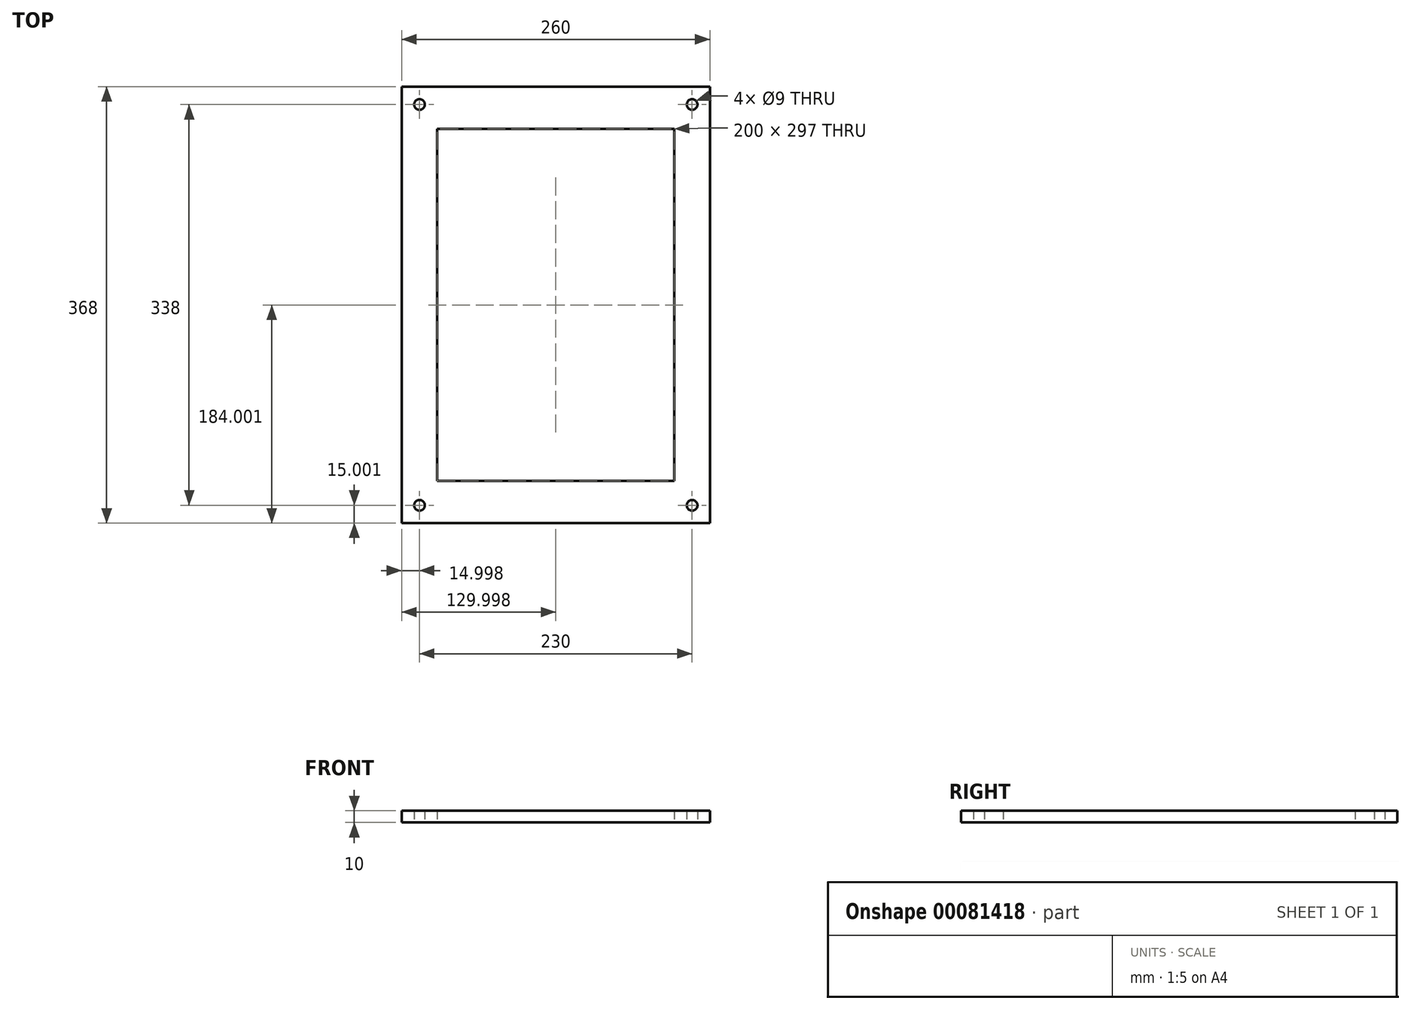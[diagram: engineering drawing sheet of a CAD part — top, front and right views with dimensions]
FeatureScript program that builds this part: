
annotation { "Feature Type Name" : "Feature", "Feature Type Description" : "" }
export const myFeature = defineFeature(function(context is Context, id is Id, definition is map)
    precondition{}
    {
        {
            var Q0;
            Q0=qCreatedBy(makeId("Top.planeOp"),FACE);
            var sketch = newSketch(context, id + "F0", { "sketchPlane" : qUnion([Q0])});
            skLineSegment(sketch, "E0.bottom", {"start": v(-243.17, -227) * mm, "end": v(16.83, -227) * mm});
            skLineSegment(sketch, "E0.top", {"start": v(-243.17, 141) * mm, "end": v(16.83, 141) * mm});
            skLineSegment(sketch, "E0.left", {"start": v(-243.17, -227) * mm, "end": v(-243.17, 141) * mm});
            skLineSegment(sketch, "E0.right", {"start": v(16.83, -227) * mm, "end": v(16.83, 141) * mm});
            skLineSegment(sketch, "E1.bottom", {"start": v(-213.17, 105.5) * mm, "end": v(-13.17, 105.5) * mm});
            skLineSegment(sketch, "E1.top", {"start": v(-213.17, -191.5) * mm, "end": v(-13.17, -191.5) * mm});
            skLineSegment(sketch, "E1.left", {"start": v(-213.17, 105.5) * mm, "end": v(-213.17, -191.5) * mm});
            skLineSegment(sketch, "E1.right", {"start": v(-13.17, 105.5) * mm, "end": v(-13.17, -191.5) * mm});
            skLineSegment(sketch, "E2", {"start": v(-113.17, 141) * mm, "end": v(-113.17, 105.5) * mm});
            skPoint(sketch, "E2.startSnap0", {"position": v(-113.17, 105.5) * mm});
            skPoint(sketch, "E2.endSnap0", {"position": v(-113.17, 105.5) * mm});
            skPoint(sketch, "E3.endSnap0", {"position": v(-13.17, -43) * mm});
            skLineSegment(sketch, "E4", {"start": v(-67.65, -227) * mm, "end": v(-67.65, -191.5) * mm});
            skCircle(sketch, "E5", {"center": v(-228.17, 126) * mm, "radius": 4.5 * mm});
            skCircle(sketch, "E6", {"center": v(1.83, 126) * mm, "radius": 4.5 * mm});
            skCircle(sketch, "E7", {"center": v(1.83, -212) * mm, "radius": 4.5 * mm});
            skCircle(sketch, "E8", {"center": v(-228.17, -212) * mm, "radius": 4.5 * mm});
            skPoint(sketch, "E9", {"position": v(-228.17, -111.12) * mm});
            skPoint(sketch, "E10", {"position": v(1.83, -43) * mm});
            skSolve(sketch);
        }
        {
            var Q0;
            Q0 = qSketchRegion(id + "F0", true);
            extrude(context, id + "F1", {"entities" : qUnion([Q0]), "depth" : 10 * mm});
        }
    });
